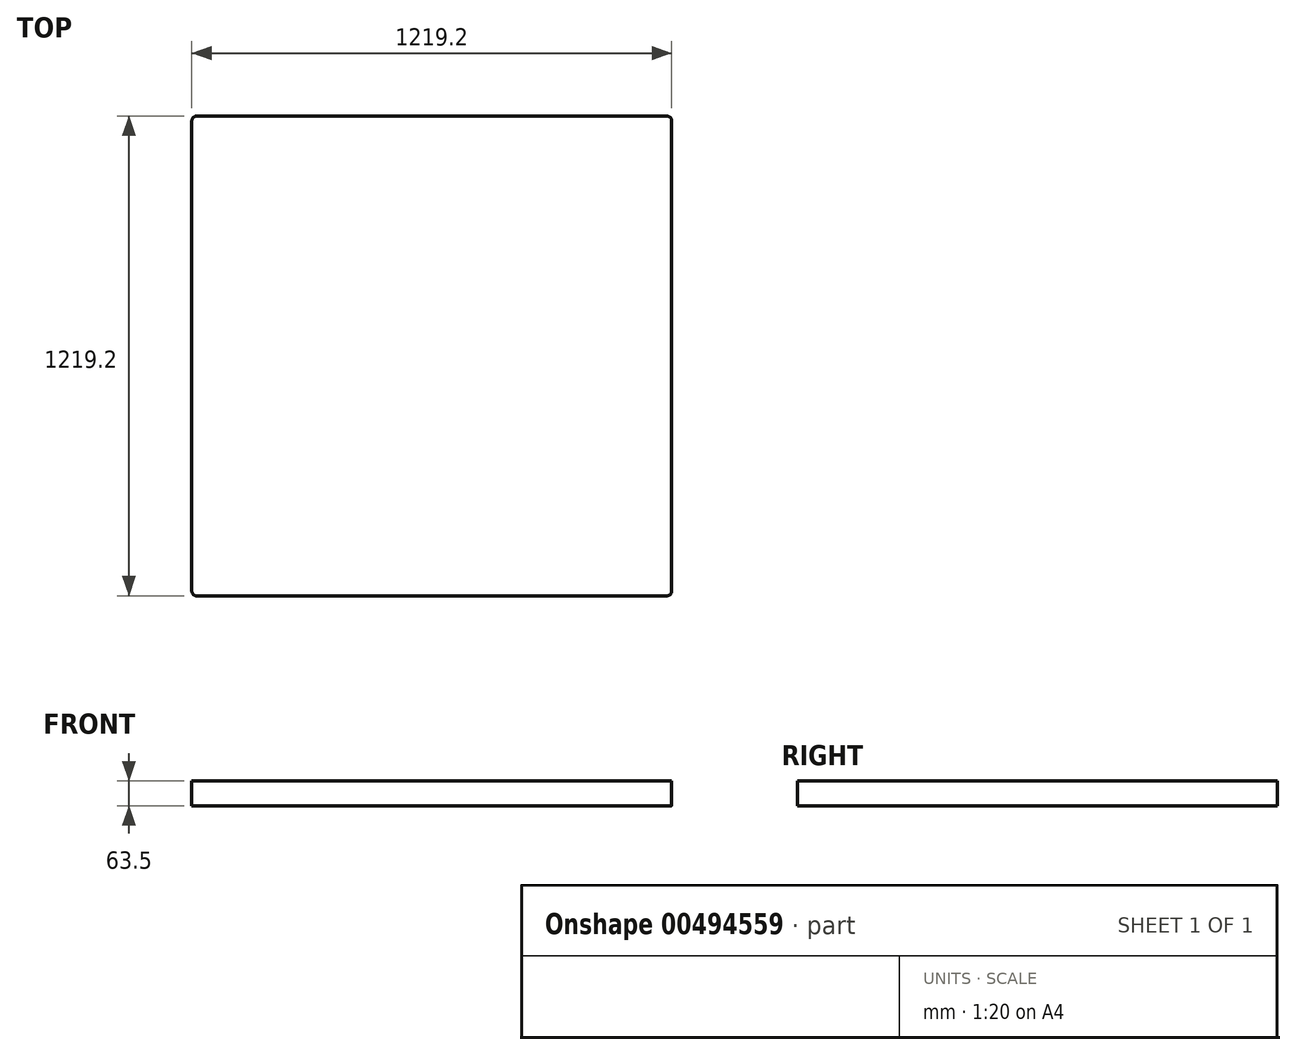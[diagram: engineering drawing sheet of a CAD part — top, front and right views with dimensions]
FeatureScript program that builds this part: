
annotation { "Feature Type Name" : "Feature", "Feature Type Description" : "" }
export const myFeature = defineFeature(function(context is Context, id is Id, definition is map)
    precondition{}
    {
        {
            var Q0;
            Q0=qCreatedBy(makeId("Top.planeOp"),FACE);
            var sketch = newSketch(context, id + "F0", { "sketchPlane" : qUnion([Q0])});
            skLineSegment(sketch, "E0.bottom", {"start": v(596.9, 609.6) * mm, "end": v(-596.9, 609.6) * mm});
            skLineSegment(sketch, "E0.top", {"start": v(596.9, -609.6) * mm, "end": v(-596.9, -609.6) * mm});
            skLineSegment(sketch, "E0.left", {"start": v(609.6, 596.9) * mm, "end": v(609.6, -596.9) * mm});
            skLineSegment(sketch, "E0.right", {"start": v(-609.6, 596.9) * mm, "end": v(-609.6, -596.9) * mm});
            skPoint(sketch, "E0.middle", {"position": v(0, 0) * mm});
            skPoint(sketch, "E1.visualSharp", {"position": v(-609.6, 609.6) * mm});
            skArc(sketch, "E1.filletArc", {"start": v(-596.9, 609.6) * mm, "mid": v(-605.88, 605.88) * mm, "end": v(-609.6, 596.9) * mm});
            skPoint(sketch, "E2.visualSharp", {"position": v(609.6, 609.6) * mm});
            skArc(sketch, "E2.filletArc", {"start": v(609.6, 596.9) * mm, "mid": v(605.88, 605.88) * mm, "end": v(596.9, 609.6) * mm});
            skPoint(sketch, "E3.visualSharp", {"position": v(609.6, -609.6) * mm});
            skArc(sketch, "E3.filletArc", {"start": v(596.9, -609.6) * mm, "mid": v(605.88, -605.88) * mm, "end": v(609.6, -596.9) * mm});
            skPoint(sketch, "E4.visualSharp", {"position": v(-609.6, -609.6) * mm});
            skArc(sketch, "E4.filletArc", {"start": v(-609.6, -596.9) * mm, "mid": v(-605.88, -605.88) * mm, "end": v(-596.9, -609.6) * mm});
            skSolve(sketch);
        }
        {
            var Q0;
            Q0=makeQuery(id+"F0.imprint","IMPRINT",FACE,{"disambiguationData":[TD([[makeQuery(id+"F0.imprint","IMPRINT",EDGE,{"derivedFrom":sQuery(id+"F0.wireOp",EDGE,"E0.bottom")}),1.0]])]});
            extrude(context, id + "F1", {"entities" : qUnion([Q0]), "depth" : 63.5 * mm});
        }
    });
